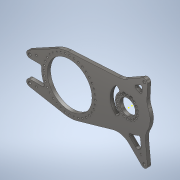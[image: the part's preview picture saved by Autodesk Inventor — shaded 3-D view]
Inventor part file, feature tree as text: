
AUTODESK INVENTOR PART (.ipt)
format: ipt  version: 2021 (Build 250183000, 183)  size: 526,336 bytes
history: native  units: in
note: dims shown in document units (in); Inventor stores cm internally (conversion verified against a paired STEP export)
features: sketch x13, extrude x10, hole x3, projected_geometry x3, chamfer x1, fillet x1
ambient origin geometry x8: Origin, YZ Plane, XZ Plane, XY Plane, X Axis, Y Axis, Z Axis, Center Point
bodies: Body1 (feature_tree)
feature tree (31):
  extrude  "Extrusion24"  Depth=2.16in
  extrude  "Extrusion28"  Depth=9.0in
  hole  "Hole9"  [1 undecoded]
  hole  "Hole11"  [1 undecoded]
  hole  "Hole13"  [1 undecoded]
  extrude  "Extrusion30"  Depth=1.5in
  extrude  "Extrusion31"  Depth=0.5in
  extrude  "Extrusion32"  Depth=0.25in
  extrude  "Extrusion33"  Depth=7.75in
  extrude  "Extrusion34"  Depth=0.25in
  chamfer  "Chamfer2"  Distance=1.0in
  sketch  "Sketch58"  dims[d289=17.223in d290=7.75in]
  extrude  "Extrusion42"  Depth=0.25in
  extrude  "Extrusion46"  Depth=0.25in
  fillet  "Fillet6"  Radius=0.3972in
  sketch  "Sketch71"  dims[d295=0.257in d296=0.75in d297=0.438in d298=0.25in d299=0.5635in d300=1.0in d301=0.8108in d302=0.1718in]
  extrude  "Extrusion50"  Depth=0.25in
  sketch  "Sketch2"  dims[d9=8.5in d92=2.16in]
  sketch  "Sketch35"  dims[d118=0.75in d119=0.75in d120=0.75in d121=0.75in d137=9.0in d142=6.5in]
  projected_geometry  "Projected Loop2"
  sketch  "Sketch36"  dims[d143=1.0in d210=1.0in]
  sketch  "Sketch40"  dims[d211=6.0in d212=6.0in]
  sketch  "Sketch43"  dims[d213=3.718in d214=1.0in]
  sketch  "Sketch47"  dims[d235=10.718in d237=1.5in]
  sketch  "Sketch48"  dims[d239=0.5in d240=0.0in d266=6.75in]
  sketch  "Sketch49"  dims[d267=0.5in d268=0.0in]
  sketch  "Sketch50"  dims[d269=0.386in d270=0.75in d271=0.762in d272=0.25in d273=0.5635in d274=0.484in d275=0.8108in d288=5.0in]
  sketch  "Sketch67"  dims[d291=3.5433in d293=360.0deg]
  sketch  "Sketch72"  dims[d303=15.0deg d316=1.0in d317=0.0481in d318=1.0in d319=0.3972in d322=0.271in d323=0.1355in d324=0.5in d325=0.266in d326=0.75in d327=0.507in d328=0.25in d329=0.5635in d330=1.0in d331=0.8108in d347=1.0in d348=0.0in d349=0.75in d350=0.75in d351=0.5in d353=0.75in d354=0.75in d355=0.25in d356=1.0in d357=0.0in d358=0.25in d359=1.0in d360=0.0in d361=1.0in d362=1.0in d363=0.25in d364=1.0in d365=0.0in d366=2.5in d367=1.0in d368=0.0in d373=0.0156in d374=0.125in d375=45.0deg d435=1.0in d436=0.0in d456=2.35in d457=8.715in d466=3.7in d467=5.25in d468=45.0deg d469=1.5in d470=1.0in d471=0.0in d472=0.25in d502=0.315in d503=1.0in d504=0.0in]
  projected_geometry  "Project Cut Edges2"
  projected_geometry  "Project Cut Edges4"
note: 3 required parameter values undecoded (feature->parameter linkage not recoverable at this tier; creation-order binding heuristic only, values carry confidence <= 0.55)
